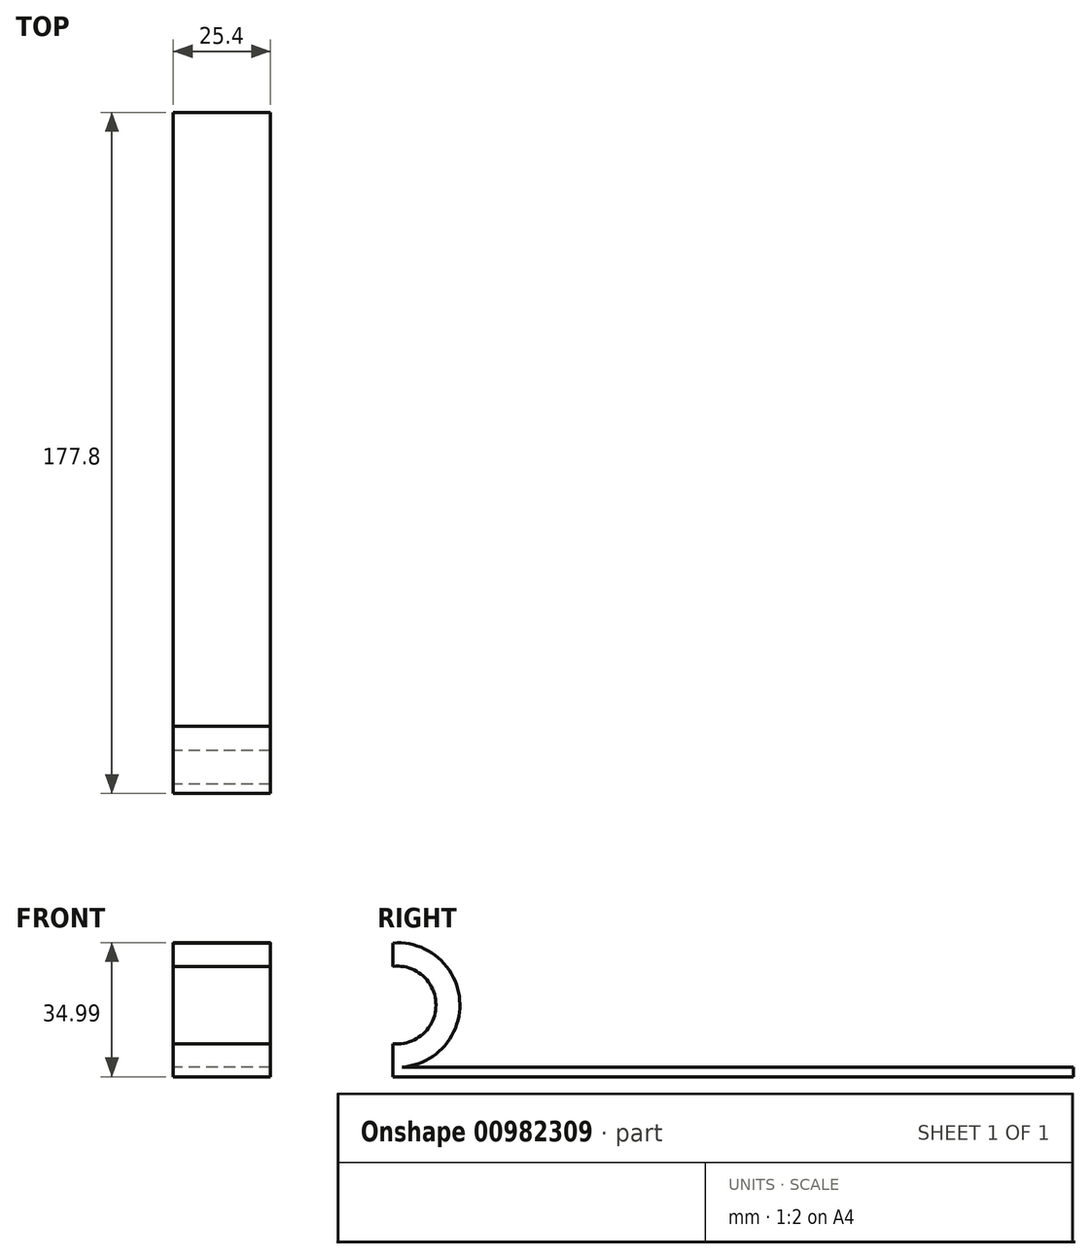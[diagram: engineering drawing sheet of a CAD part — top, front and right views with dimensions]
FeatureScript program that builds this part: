
annotation { "Feature Type Name" : "Feature", "Feature Type Description" : "" }
export const myFeature = defineFeature(function(context is Context, id is Id, definition is map)
    precondition{}
    {
        {
            var Q0;
            Q0=qCreatedBy(makeId("Top.planeOp"),FACE);
            var sketch = newSketch(context, id + "F0", { "sketchPlane" : qUnion([Q0])});
            skLineSegment(sketch, "E0.bottom", {"start": v(-63.88, 122.46) * mm, "end": v(-38.48, 122.46) * mm});
            skLineSegment(sketch, "E0.top", {"start": v(-63.88, -55.34) * mm, "end": v(-38.48, -55.34) * mm});
            skLineSegment(sketch, "E0.left", {"start": v(-63.88, 122.46) * mm, "end": v(-63.88, -55.34) * mm});
            skLineSegment(sketch, "E0.right", {"start": v(-38.48, 122.46) * mm, "end": v(-38.48, -55.34) * mm});
            skSolve(sketch);
        }
        {
            var Q0;
            Q0=makeQuery(id+"F0.imprint","IMPRINT",FACE,{"disambiguationData":[TD([[makeQuery(id+"F0.imprint","IMPRINT",EDGE,{"derivedFrom":sQuery(id+"F0.wireOp",EDGE,"E0.bottom")}),-1.0]])]});
            extrude(context, id + "F1", {"entities" : qUnion([Q0]), "depth" : 2.54 * mm, "offsetDistance" : 25.4 * mm});
        }
        {
            var Q0;
            Q0=makeQuery(id+"F1.opExtrude","CAP_EDGE",EDGE,{"disambiguationData":[OSD([sQuery(id+"F0.wireOp",EDGE,"E0.left")])],"isStart":false});
            cPlane(context, id + "F2", {"entities" : qUnion([Q0]), "cplaneType" : CPlaneType.LINE_ANGLE, "offset" : 25.4 * mm, "angle" : 90 * degree, "width" : 152.4 * mm, "height" : 152.4 * mm});
        }
        {
            var Q0;
            Q0=qCreatedBy(id+"F2.planeOp",FACE);
            var sketch = newSketch(context, id + "F3", { "sketchPlane" : qUnion([Q0])});
            skPoint(sketch, "E1.0", {"position": v(-55.34, 2.54) * mm});
            skArc(sketch, "E2", {"start": v(-55.34, 2.54) * mm, "mid": v(-37.87, 18.74) * mm, "end": v(-55.34, 34.94) * mm});
            skLineSegment(sketch, "E3", {"start": v(-55.34, 2.54) * mm, "end": v(-55.34, 34.94) * mm});
            skArc(sketch, "E4", {"start": v(-55.34, 8.64) * mm, "mid": v(-44.1, 18.74) * mm, "end": v(-55.34, 28.84) * mm});
            skSolve(sketch);
        }
        {
            var Q0;
            {var subQ0=sQuery(id+"F3.wireOp",EDGE,"E2");Q0=makeQuery(id+"F3.imprint","IMPRINT",FACE,{"disambiguationData":[TD([[makeQuery(id+"F3.imprint","IMPRINT",EDGE,{"derivedFrom":subQ0}),1.0]])]});}
            extrude(context, id + "F4", {"entities" : qUnion([Q0]), "operationType" : NewBodyOperationType.ADD, "depth" : 25.4 * mm, "offsetDistance" : 25.4 * mm});
        }
    });
